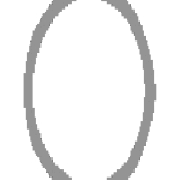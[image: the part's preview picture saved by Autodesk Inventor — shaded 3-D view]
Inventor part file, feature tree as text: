
AUTODESK INVENTOR PART (.ipt)
format: ipt  version: 2021 (Build 250183000, 183)  size: 109,056 bytes
history: native  units: in
note: dims shown in document units (in); Inventor stores cm internally (conversion verified against a paired STEP export)
features: other x4, sketch x3, plane x1
ambient origin geometry x8: Origin, YZ Plane, XZ Plane, XY Plane, X Axis, Y Axis, Z Axis, Center Point
bodies: Solid1 (feature_tree), Body (feature_tree)
feature tree (8):
  other  "Driven Length"
  other  "Frame Generator"
  other  "Start Plane"
  other  "End Plane"
  sketch  "Sketch"  dims[d2=37.0212in d4=-0.0in d5=37.0212in d6=0.12in d7=0.0in d8=90.0deg d9=37.0212in]
  sketch  "Sketch2"  dims[d0=1.0in]
  plane  "Work Plane3"
  sketch  "Sketch3"  dims[d1=0.065in]
